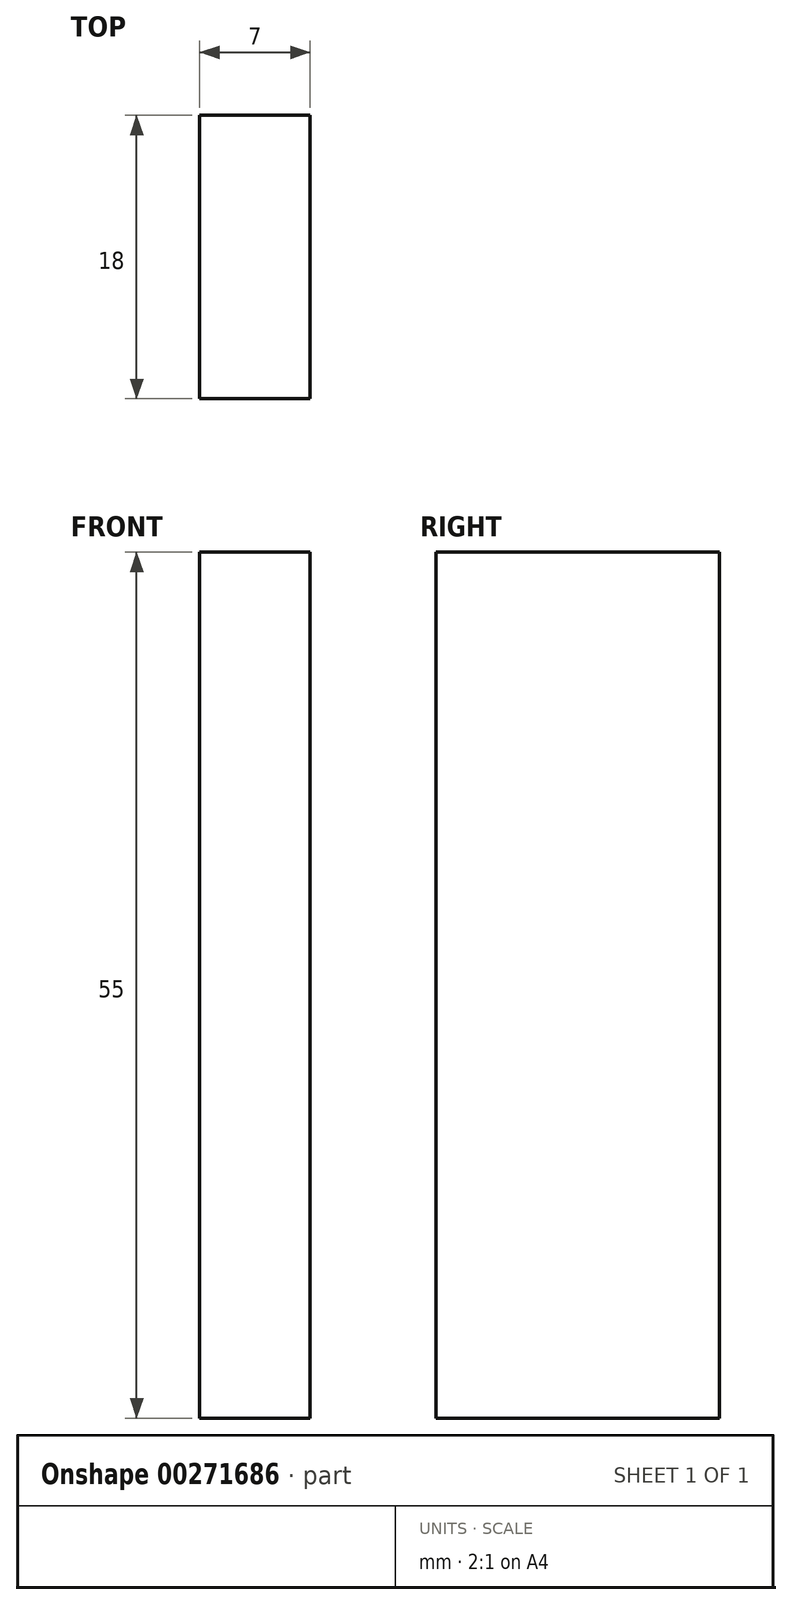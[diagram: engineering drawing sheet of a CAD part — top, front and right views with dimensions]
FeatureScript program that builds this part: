
annotation { "Feature Type Name" : "Feature", "Feature Type Description" : "" }
export const myFeature = defineFeature(function(context is Context, id is Id, definition is map)
    precondition{}
    {
        {
            var Q0;
            Q0=qCreatedBy(makeId("Front.planeOp"),FACE);
            var sketch = newSketch(context, id + "F0", { "sketchPlane" : qUnion([Q0])});
            skLineSegment(sketch, "E0.bottom", {"start": v(3.5, 27.5) * mm, "end": v(-3.5, 27.5) * mm});
            skLineSegment(sketch, "E0.top", {"start": v(3.5, -27.5) * mm, "end": v(-3.5, -27.5) * mm});
            skLineSegment(sketch, "E0.left", {"start": v(3.5, 27.5) * mm, "end": v(3.5, -27.5) * mm});
            skLineSegment(sketch, "E0.right", {"start": v(-3.5, 27.5) * mm, "end": v(-3.5, -27.5) * mm});
            skPoint(sketch, "E0.middle", {"position": v(0, 0) * mm});
            skSolve(sketch);
        }
        {
            var Q0;
            Q0=makeQuery(id+"F0.imprint","IMPRINT",FACE,{"disambiguationData":[TD([[makeQuery(id+"F0.imprint","IMPRINT",EDGE,{"derivedFrom":sQuery(id+"F0.wireOp",EDGE,"E0.bottom")}),1.0]])]});
            extrude(context, id + "F1", {"entities" : qUnion([Q0]), "depth" : 18 * mm});
        }
    });
